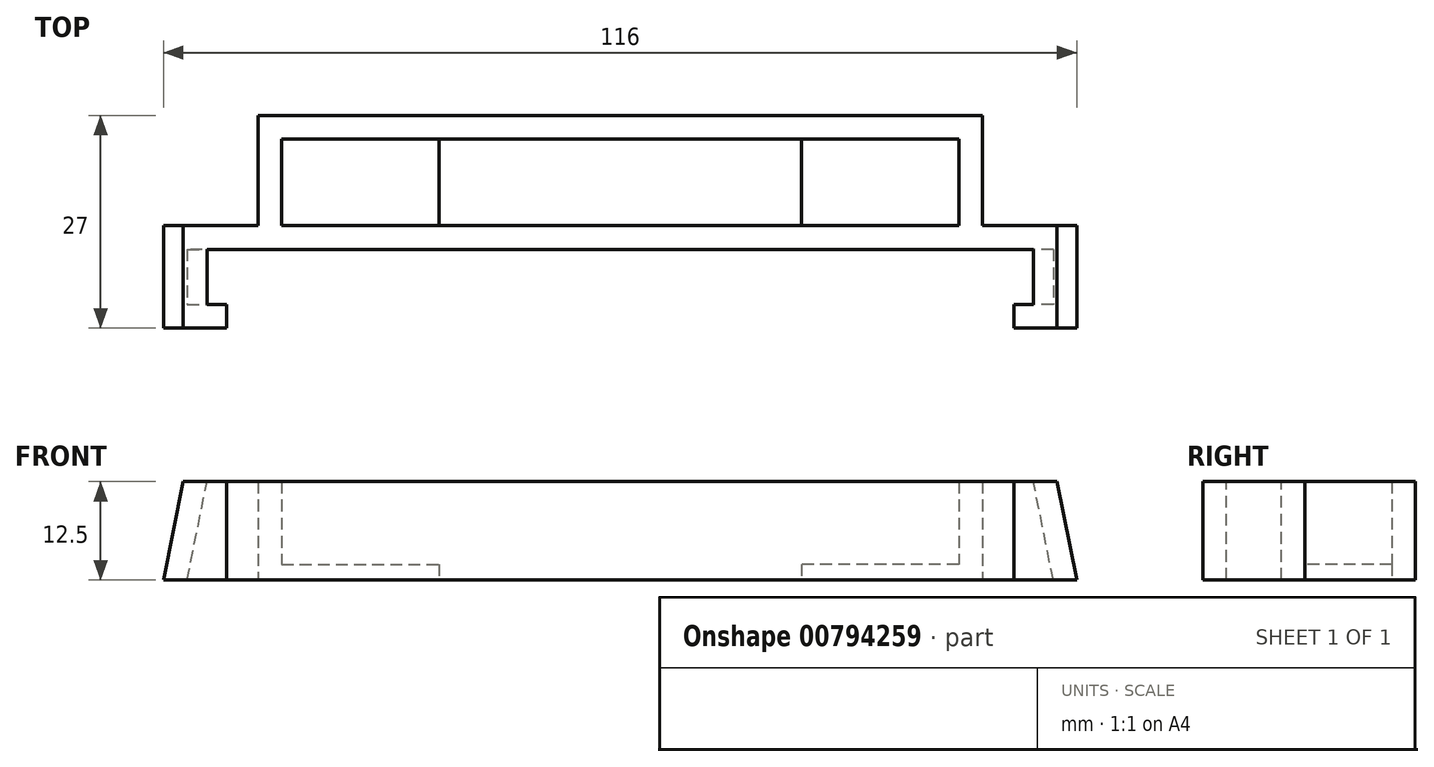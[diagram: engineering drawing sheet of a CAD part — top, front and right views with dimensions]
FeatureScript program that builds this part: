
annotation { "Feature Type Name" : "Feature", "Feature Type Description" : "" }
export const myFeature = defineFeature(function(context is Context, id is Id, definition is map)
    precondition{}
    {
        {
            var Q0;
            Q0=qCreatedBy(makeId("Top.planeOp"),FACE);
            var sketch = newSketch(context, id + "F0", { "sketchPlane" : qUnion([Q0])});
            skLineSegment(sketch, "E0", {"start": v(0, 20.9) * mm, "end": v(-55, 20.9) * mm});
            skLineSegment(sketch, "E1", {"start": v(-55, 20.9) * mm, "end": v(-55, 13.9) * mm});
            skLineSegment(sketch, "E2", {"start": v(-55, 13.9) * mm, "end": v(-50, 13.9) * mm});
            skLineSegment(sketch, "E3.0", {"start": v(-58, 10.9) * mm, "end": v(-50, 10.9) * mm});
            skLineSegment(sketch, "E3.1", {"start": v(-58, 23.9) * mm, "end": v(-58, 10.9) * mm});
            skLineSegment(sketch, "E3.2", {"start": v(0, 23.9) * mm, "end": v(-58, 23.9) * mm});
            skLineSegment(sketch, "E4", {"start": v(0, 23.9) * mm, "end": v(0, 20.9) * mm});
            skLineSegment(sketch, "E5", {"start": v(-50, 13.9) * mm, "end": v(-50, 10.9) * mm});
            skLineSegment(sketch, "E6.MirrorCS", {"start": v(0, 23.9) * mm, "end": v(58, 23.9) * mm});
            skLineSegment(sketch, "E7.MirrorCS", {"start": v(50, 13.9) * mm, "end": v(50, 10.9) * mm});
            skLineSegment(sketch, "E8.MirrorCS", {"start": v(58, 23.9) * mm, "end": v(58, 10.9) * mm});
            skLineSegment(sketch, "E9.MirrorCS", {"start": v(58, 10.9) * mm, "end": v(50, 10.9) * mm});
            skLineSegment(sketch, "E10.MirrorCS", {"start": v(55, 13.9) * mm, "end": v(50, 13.9) * mm});
            skLineSegment(sketch, "E11.MirrorCS", {"start": v(55, 20.9) * mm, "end": v(55, 13.9) * mm});
            skLineSegment(sketch, "E12.MirrorCS", {"start": v(0, 20.9) * mm, "end": v(55, 20.9) * mm});
            skSolve(sketch);
        }
        {
            var Q0;
            Q0=qCreatedBy(makeId("Top.planeOp"),FACE);
            cPlane(context, id + "F1", {"entities" : qUnion([Q0]), "cplaneType" : CPlaneType.OFFSET, "offset" : 25 * mm / 2, "width" : 150 * mm, "height" : 150 * mm});
        }
        {
            var Q0;
            Q0=qCreatedBy(id+"F1.planeOp",FACE);
            var sketch = newSketch(context, id + "F2", { "sketchPlane" : qUnion([Q0])});
            skLineSegment(sketch, "E13", {"start": v(0, 20.9) * mm, "end": v(-52.5, 20.9) * mm});
            skLineSegment(sketch, "E14", {"start": v(-52.5, 20.9) * mm, "end": v(-52.5, 13.9) * mm});
            skLineSegment(sketch, "E15", {"start": v(-52.5, 13.9) * mm, "end": v(-50, 13.9) * mm});
            skLineSegment(sketch, "E16.0", {"start": v(-55.5, 10.9) * mm, "end": v(-50, 10.9) * mm});
            skLineSegment(sketch, "E16.1", {"start": v(-55.5, 23.9) * mm, "end": v(-55.5, 10.9) * mm});
            skLineSegment(sketch, "E16.2", {"start": v(0, 23.9) * mm, "end": v(-55.5, 23.9) * mm});
            skLineSegment(sketch, "E17", {"start": v(-50, 13.9) * mm, "end": v(-50, 10.9) * mm});
            skLineSegment(sketch, "E18", {"start": v(0, 23.9) * mm, "end": v(0, 20.9) * mm});
            skLineSegment(sketch, "E19.MirrorCS", {"start": v(52.5, 13.9) * mm, "end": v(50, 13.9) * mm});
            skLineSegment(sketch, "E20.MirrorCS", {"start": v(52.5, 20.9) * mm, "end": v(52.5, 13.9) * mm});
            skLineSegment(sketch, "E21.MirrorCS", {"start": v(0, 23.9) * mm, "end": v(55.5, 23.9) * mm});
            skLineSegment(sketch, "E22.MirrorCS", {"start": v(55.5, 10.9) * mm, "end": v(50, 10.9) * mm});
            skLineSegment(sketch, "E23.MirrorCS", {"start": v(0, 20.9) * mm, "end": v(52.5, 20.9) * mm});
            skLineSegment(sketch, "E24.MirrorCS", {"start": v(50, 13.9) * mm, "end": v(50, 10.9) * mm});
            skLineSegment(sketch, "E25.MirrorCS", {"start": v(55.5, 23.9) * mm, "end": v(55.5, 10.9) * mm});
            skSolve(sketch);
        }
        {
            var Q0;
            Q0 = qSketchRegion(id + "F0", true);
            var Q1;
            Q1 = qSketchRegion(id + "F2", true);
            loft(context, id + "F3", {"sheetProfilesArray" : [{ "sheetProfileEntities" : qUnion([Q0]) }, { "sheetProfileEntities" : qUnion([Q1]) }]});
        }
        {
            var Q0;
            Q0=qCreatedBy(makeId("Top.planeOp"),FACE);
            var sketch = newSketch(context, id + "F4", { "sketchPlane" : qUnion([Q0])});
            skLineSegment(sketch, "E26", {"start": v(0, 34.9) * mm, "end": v(-43, 34.9) * mm});
            skLineSegment(sketch, "E27", {"start": v(-43, 34.9) * mm, "end": v(-43, 23.9) * mm});
            skLineSegment(sketch, "E28.0", {"start": v(-46, 37.9) * mm, "end": v(-46, 23.9) * mm});
            skLineSegment(sketch, "E28.1", {"start": v(0, 37.9) * mm, "end": v(-46, 37.9) * mm});
            skLineSegment(sketch, "E29", {"start": v(-46, 23.9) * mm, "end": v(-43, 23.9) * mm});
            skLineSegment(sketch, "E30", {"start": v(0, 37.9) * mm, "end": v(0, 34.9) * mm});
            skLineSegment(sketch, "E31.MirrorCS", {"start": v(0, 37.9) * mm, "end": v(46, 37.9) * mm});
            skLineSegment(sketch, "E32.MirrorCS", {"start": v(46, 23.9) * mm, "end": v(43, 23.9) * mm});
            skLineSegment(sketch, "E33.MirrorCS", {"start": v(46, 37.9) * mm, "end": v(46, 23.9) * mm});
            skLineSegment(sketch, "E34.MirrorCS", {"start": v(43, 34.9) * mm, "end": v(43, 23.9) * mm});
            skLineSegment(sketch, "E35.MirrorCS", {"start": v(0, 34.9) * mm, "end": v(43, 34.9) * mm});
            skLineSegment(sketch, "E36.bottom", {"start": v(-43, 34.9) * mm, "end": v(-23, 34.9) * mm});
            skLineSegment(sketch, "E36.top", {"start": v(-43, 23.9) * mm, "end": v(-23, 23.9) * mm});
            skLineSegment(sketch, "E36.right", {"start": v(-23, 34.9) * mm, "end": v(-23, 23.9) * mm});
            skLineSegment(sketch, "E37.MirrorCS", {"start": v(43, 34.9) * mm, "end": v(23, 34.9) * mm});
            skLineSegment(sketch, "E38.MirrorCS", {"start": v(43, 23.9) * mm, "end": v(23, 23.9) * mm});
            skLineSegment(sketch, "E39.MirrorCS", {"start": v(23, 34.9) * mm, "end": v(23, 23.9) * mm});
            skSolve(sketch);
        }
        {
            var Q0;
            {var subQ0=sQuery(id+"F4.wireOp",EDGE,"E27");Q0=makeQuery(id+"F4.imprint","IMPRINT",FACE,{"disambiguationData":[TD([[makeQuery(id+"F4.imprint","IMPRINT",EDGE,{"derivedFrom":subQ0}),1.0]])]});}
            var Q1;
            {var subQ0=sQuery(id+"F4.wireOp",EDGE,"E34.MirrorCS");Q1=makeQuery(id+"F4.imprint","IMPRINT",FACE,{"disambiguationData":[TD([[makeQuery(id+"F4.imprint","IMPRINT",EDGE,{"derivedFrom":subQ0}),-1.0]])]});}
            extrude(context, id + "F5", {"entities" : qUnion([Q0, Q1]), "operationType" : NewBodyOperationType.ADD, "depth" : 2 * mm, "offsetDistance" : 25 * mm});
        }
        {
            var Q0;
            {var subQ0=sQuery(id+"F4.wireOp",EDGE,"E27");Q0=makeQuery(id+"F4.imprint","IMPRINT",FACE,{"disambiguationData":[TD([[makeQuery(id+"F4.imprint","IMPRINT",EDGE,{"derivedFrom":subQ0}),-1.0]])]});}
            var Q1;
            {var subQ0=sQuery(id+"F4.wireOp",EDGE,"E30");Q1=makeQuery(id+"F4.imprint","IMPRINT",FACE,{"disambiguationData":[TD([[makeQuery(id+"F4.imprint","IMPRINT",EDGE,{"derivedFrom":subQ0}),1.0]])]});}
            extrude(context, id + "F6", {"entities" : qUnion([Q0, Q1]), "operationType" : NewBodyOperationType.ADD, "depth" : 25 * mm / 2, "offsetDistance" : 25 * mm});
        }
    });
